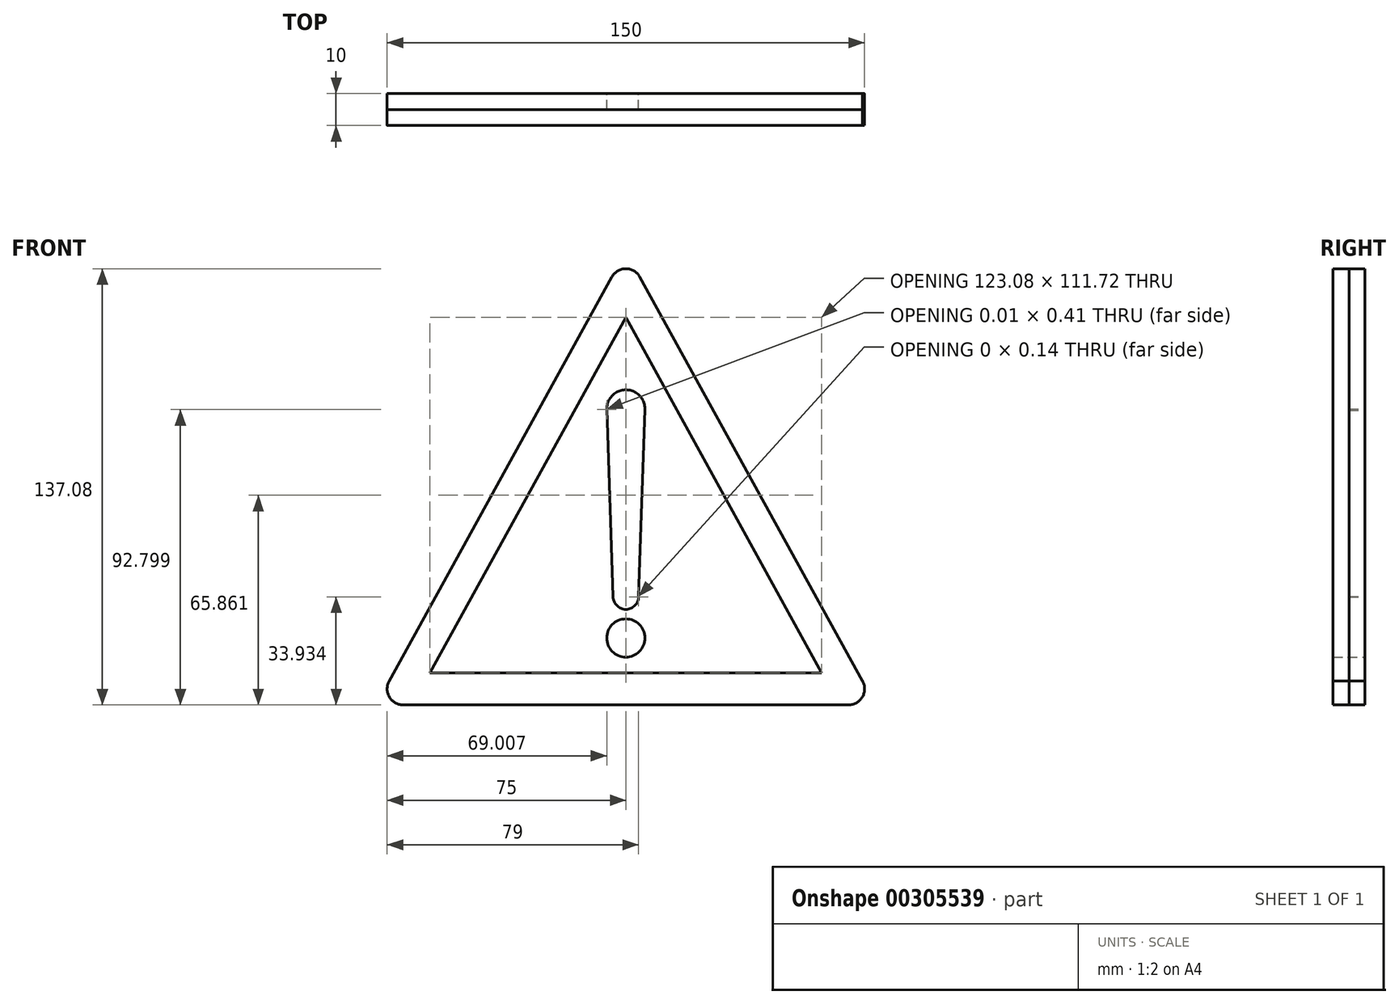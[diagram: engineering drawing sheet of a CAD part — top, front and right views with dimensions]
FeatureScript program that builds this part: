
annotation { "Feature Type Name" : "Feature", "Feature Type Description" : "" }
export const myFeature = defineFeature(function(context is Context, id is Id, definition is map)
    precondition{}
    {
        {
            var Q0;
            Q0=qCreatedBy(makeId("Front.planeOp"),FACE);
            var sketch = newSketch(context, id + "F0", { "sketchPlane" : qUnion([Q0])});
            skLineSegment(sketch, "E0", {"start": v(0, 32.36) * mm, "end": v(0, 15.9) * mm, "construction": true});
            skArc(sketch, "E1", {"start": v(-74.38, -69.69) * mm, "mid": v(-74.3, -74.64) * mm, "end": v(-70, -77.1) * mm});
            skArc(sketch, "E2", {"start": v(70, -77.1) * mm, "mid": v(74.35, -74.57) * mm, "end": v(74.3, -69.54) * mm});
            skLineSegment(sketch, "E3", {"start": v(-70, -77.1) * mm, "end": v(70, -77.1) * mm});
            skLineSegment(sketch, "E4", {"start": v(74.3, -69.54) * mm, "end": v(74.34, -69.61) * mm});
            skPoint(sketch, "E5.center.orphan", {"position": v(0, 37.36) * mm});
            skArc(sketch, "E6", {"start": v(4.38, 57.4) * mm, "mid": v(0, 59.98) * mm, "end": v(-4.38, 57.4) * mm});
            skLineSegment(sketch, "E7", {"start": v(-74.38, -69.69) * mm, "end": v(-4.38, 57.4) * mm});
            skLineSegment(sketch, "E8", {"start": v(4.38, 57.4) * mm, "end": v(74.38, -69.69) * mm});
            skLineSegment(sketch, "E9.0", {"start": v(-61.54, -67.1) * mm, "end": v(0, 44.62) * mm});
            skLineSegment(sketch, "E10.0", {"start": v(0, 44.62) * mm, "end": v(61.54, -67.1) * mm});
            skLineSegment(sketch, "E11.0", {"start": v(-61.54, -67.1) * mm, "end": v(61.54, -67.1) * mm});
            skArc(sketch, "E12", {"start": v(6, 15.7) * mm, "mid": v(-0.1, 21.9) * mm, "end": v(-5.99, 15.5) * mm});
            skCircle(sketch, "E13", {"center": v(0, -56.1) * mm, "radius": 6 * mm});
            skArc(sketch, "E14", {"start": v(-4, -43.1) * mm, "mid": v(0, -47.1) * mm, "end": v(4, -43.1) * mm});
            skLineSegment(sketch, "E15", {"start": v(-6, 15.9) * mm, "end": v(-4, -43.1) * mm});
            skLineSegment(sketch, "E16", {"start": v(4, -43.23) * mm, "end": v(6, 15.7) * mm});
            skLineSegment(sketch, "E17.trimOffspring", {"start": v(4, -43.1) * mm, "end": v(4, -43.1) * mm});
            skPoint(sketch, "E18.0.start.orphan", {"position": v(-70, 15.9) * mm});
            skLineSegment(sketch, "E19.trimOffspring", {"start": v(-4, -43.1) * mm, "end": v(-4, -43.1) * mm});
            skPoint(sketch, "E20.orphan", {"position": v(-70, -43.1) * mm});
            skPoint(sketch, "E21.0.start.orphan", {"position": v(-70, -56.1) * mm});
            skPoint(sketch, "E22.orphan", {"position": v(70, 15.9) * mm});
            skPoint(sketch, "E23.trimOffspring.end.orphan", {"position": v(70, -43.1) * mm});
            skPoint(sketch, "E24.trimOffspring.end.orphan", {"position": v(70, -56.1) * mm});
            skLineSegment(sketch, "E25.trimOffspring", {"start": v(0, -43.1) * mm, "end": v(0, -50.1) * mm, "construction": true});
            skLineSegment(sketch, "E26.trimOffspring", {"start": v(-70, -56.1) * mm, "end": v(-70, -70.16) * mm, "construction": true});
            skLineSegment(sketch, "E27.trimOffspring", {"start": v(75, -72.1) * mm, "end": v(75.82, -72.1) * mm, "construction": true});
            skLineSegment(sketch, "E28.trimOffspring", {"start": v(0, -62.1) * mm, "end": v(0, -70.16) * mm, "construction": true});
            skSolve(sketch);
        }
        {
            var Q0;
            {var subQ0=sQuery(id+"F0.wireOp",EDGE,"E4");Q0=makeQuery(id+"F0.imprint","IMPRINT",FACE,{"disambiguationData":[TD([[makeQuery(id+"F0.imprint","IMPRINT",EDGE,{"derivedFrom":subQ0}),-1.0]])]});}
            var Q1;
            Q1=makeQuery(id+"F0.imprint","IMPRINT",FACE,{"disambiguationData":[TD([[makeQuery(id+"F0.imprint","IMPRINT",EDGE,{"derivedFrom":sQuery(id+"F0.wireOp",EDGE,"E9.0")}),-1.0]])]});
            var Q2;
            Q2=makeQuery(id+"F0.imprint","IMPRINT",FACE,{"disambiguationData":[TD([[makeQuery(id+"F0.imprint","IMPRINT",EDGE,{"derivedFrom":sQuery(id+"F0.wireOp",EDGE,"E13")}),1.0]])]});
            var Q3;
            {var subQ0=sQuery(id+"F0.wireOp",EDGE,"E17.trimOffspring");Q3=makeQuery(id+"F0.imprint","IMPRINT",FACE,{"disambiguationData":[TD([[makeQuery(id+"F0.imprint","IMPRINT",EDGE,{"derivedFrom":subQ0}),1.0]])]});}
            var Q4;
            Q4=makeQuery(id+"F0.imprint","IMPRINT",FACE,{"disambiguationData":[TD([[makeQuery(id+"F0.imprint","IMPRINT",EDGE,{"derivedFrom":sQuery(id+"F0.wireOp",EDGE,"E1")}),1.0]])]});
            extrude(context, id + "F1", {"entities" : qUnion([Q0, Q1, Q2, Q3, Q4]), "depth" : 5 * mm});
        }
        {
            var Q0;
            {var subQ0=sQuery(id+"F0.wireOp",EDGE,"E17.trimOffspring");Q0=makeQuery(id+"F0.imprint","IMPRINT",FACE,{"disambiguationData":[TD([[makeQuery(id+"F0.imprint","IMPRINT",EDGE,{"derivedFrom":subQ0}),1.0]])]});}
            var Q1;
            Q1=makeQuery(id+"F0.imprint","IMPRINT",FACE,{"disambiguationData":[TD([[makeQuery(id+"F0.imprint","IMPRINT",EDGE,{"derivedFrom":sQuery(id+"F0.wireOp",EDGE,"E13")}),1.0]])]});
            var Q2;
            Q2=makeQuery(id+"F0.imprint","IMPRINT",FACE,{"disambiguationData":[TD([[makeQuery(id+"F0.imprint","IMPRINT",EDGE,{"derivedFrom":sQuery(id+"F0.wireOp",EDGE,"E1")}),1.0]])]});
            extrude(context, id + "F2", {"entities" : qUnion([Q0, Q1, Q2]), "depth" : 10 * mm});
        }
    });
